FCSTD DOCUMENT  (FreeCAD 0.20R29410 (Git))
Label: quattro spacer
License: All rights reserved
LicenseURL: http://en.wikipedia.org/wiki/All_rights_reserved
objects: Sketcher::SketchObject×1, PartDesign::Body×1, TechDraw::DrawSVGTemplate×1, TechDraw::DrawViewSymbol×1, TechDraw::DrawPage×1
note: 2 computed .brp shape members not serialized (recipe doc carries the construction recipe); baked Part::Feature solids carry a one-line shape summary decoded from their .brp

FEATURE [Sketcher::SketchObject] Sketch
  FullyConstrained = true
  MapMode = 5
  Support = -> [XY_Plane]
  sketch-geometry (8):
    g0: LineSegment StartX=-15 StartY=-120.5 StartZ=0 EndX=-15 EndY=120.5 EndZ=0
    g1: LineSegment StartX=-15 StartY=120.5 StartZ=0 EndX=15 EndY=120.5 EndZ=0
    g2: LineSegment StartX=15 StartY=120.5 StartZ=0 EndX=15 EndY=-120.5 EndZ=0
    g3: LineSegment StartX=15 StartY=-120.5 StartZ=0 EndX=-15 EndY=-120.5 EndZ=0
    g4: GeomPoint X=0 Y=0 Z=0
    g5: Circle CenterX=-3 CenterY=-84.5 CenterZ=0 NormalX=0 NormalY=0 NormalZ=1 AngleXU=0 Radius=4
    g6: Circle CenterX=-3 CenterY=85.5 CenterZ=0 NormalX=0 NormalY=0 NormalZ=1 AngleXU=0 Radius=4
    g7: LineSegment StartX=-3 StartY=120.5 StartZ=0 EndX=-3 EndY=-120.5 EndZ=0
  constraints (22):
    c: Coincident(g0,g1)
    c: Coincident(g1,g2)
    c: Coincident(g2,g3)
    c: Coincident(g3,g0)
    c: Horizontal(g1)
    c: Horizontal(g3)
    c: Vertical(g0)
    c: Vertical(g2)
    c: Symmetric(g1,g0,g4)
    c: Coincident(g4,g-1)
    c: DistanceY(g0,g0) = 241
    c: DistanceY(g6,g0) = 35
    c: Diameter(g6) = 8
    c: DistanceY(g5,g6) = 170
    c: DistanceX(g1,g1) = 30
    c: PointOnObject(g7,g1)
    c: PointOnObject(g7,g3)
    c: Vertical(g7)
    c: DistanceX(g0,g7) = 12
    c: PointOnObject(g6,g7)
    c: PointOnObject(g5,g7)
    c: Equal(g5,g6)
FEATURE [PartDesign::Body] Body
  Group = -> [Sketch]
  Origin = -> Origin
FEATURE [TechDraw::DrawSVGTemplate] Template
  EditableTexts = Designed_by_Name=Designed by Name; Drawing_number=Drawing number; FC-Date=Date; FC-SC=Scale; FC-SH=Sheet; FC-Title=Title; Subtitle=Subtitle; Weight=Weight
  Height = 210
  Orientation = 1
  Width = 297
FEATURE [TechDraw::DrawViewSymbol] ActiveView
  LockPosition = false
  Rotation = 0
  ScaleType = 2
  X = 148.5
  Y = 105
FEATURE [TechDraw::DrawPage] Page
  KeepUpdated = true
  NextBalloonIndex = 1
  ProjectionType = 0
  Template = -> Template
  Views = -> [ActiveView]
